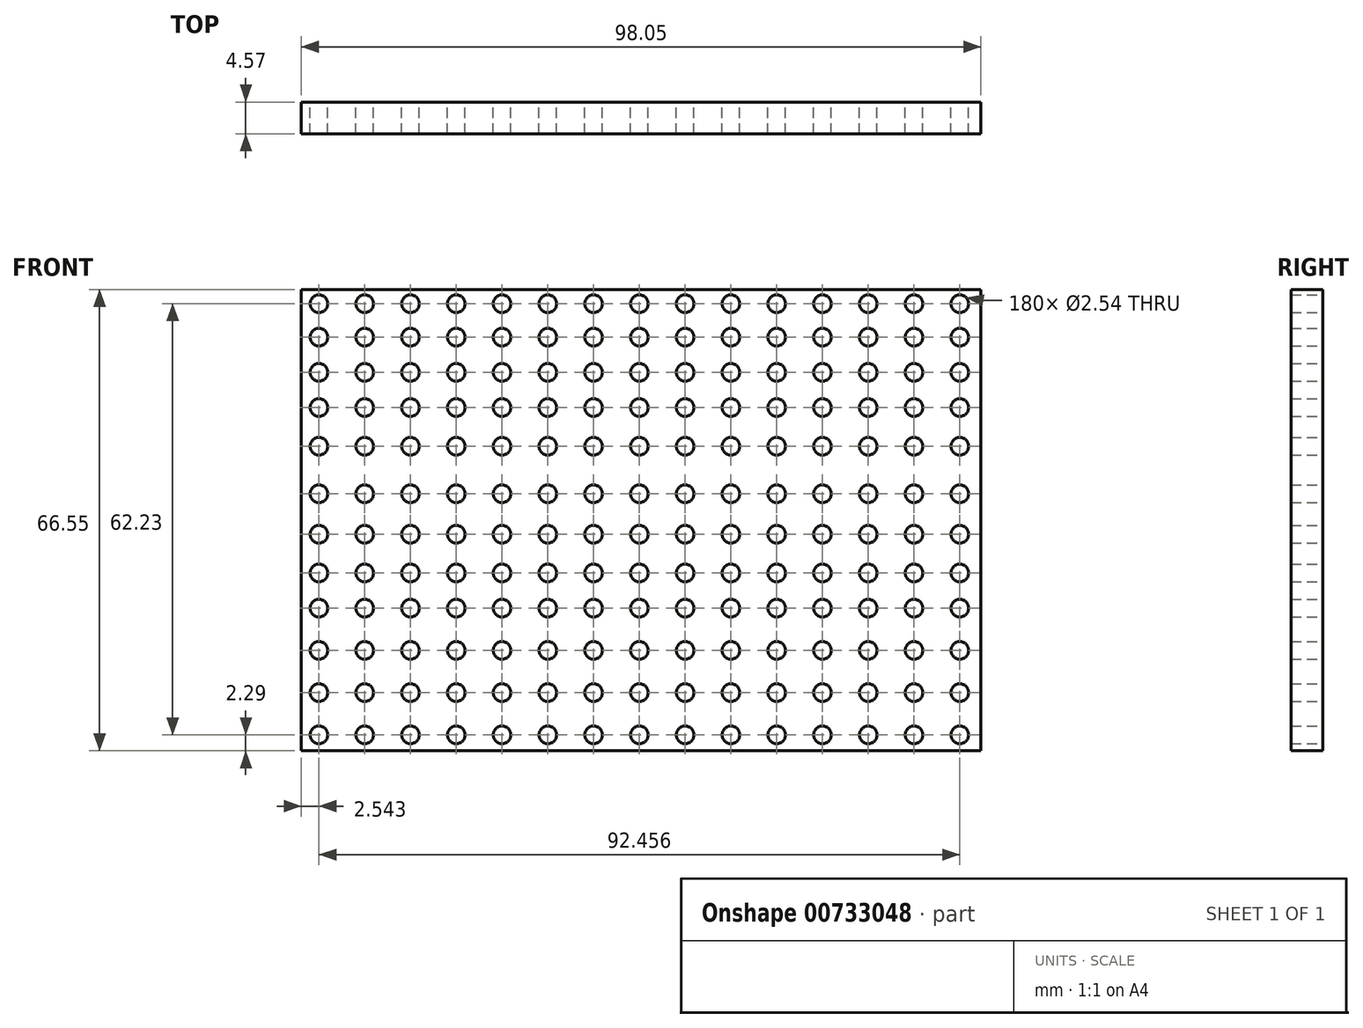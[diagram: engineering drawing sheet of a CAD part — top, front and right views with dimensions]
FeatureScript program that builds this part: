
annotation { "Feature Type Name" : "Feature", "Feature Type Description" : "" }
export const myFeature = defineFeature(function(context is Context, id is Id, definition is map)
    precondition{}
    {
        {
            var Q0;
            Q0=qCreatedBy(makeId("Front.planeOp"),FACE);
            var sketch = newSketch(context, id + "F0", { "sketchPlane" : qUnion([Q0])});
            skLineSegment(sketch, "E0.bottom", {"start": v(-48.39, 32.38) * mm, "end": v(49.66, 32.38) * mm});
            skLineSegment(sketch, "E0.top", {"start": v(-48.39, -34.17) * mm, "end": v(49.66, -34.17) * mm});
            skLineSegment(sketch, "E0.left", {"start": v(-48.39, 32.38) * mm, "end": v(-48.39, -34.17) * mm});
            skLineSegment(sketch, "E0.right", {"start": v(49.66, 32.38) * mm, "end": v(49.66, -34.17) * mm});
            skCircle(sketch, "E1", {"center": v(-45.85, 30.35) * mm, "radius": 1.27 * mm});
            skCircle(sketch, "E2.0.1.0", {"center": v(-45.85, -31.88) * mm, "radius": 1.27 * mm});
            skCircle(sketch, "E2.1.0.0", {"center": v(-39.24, 30.35) * mm, "radius": 1.27 * mm});
            skCircle(sketch, "E2.1.1.0", {"center": v(-39.24, -31.88) * mm, "radius": 1.27 * mm});
            skCircle(sketch, "E2.2.0.0", {"center": v(-32.64, 30.35) * mm, "radius": 1.27 * mm});
            skCircle(sketch, "E2.2.1.0", {"center": v(-32.64, -31.88) * mm, "radius": 1.27 * mm});
            skCircle(sketch, "E2.3.0.0", {"center": v(-26.04, 30.35) * mm, "radius": 1.27 * mm});
            skCircle(sketch, "E2.3.1.0", {"center": v(-26.04, -31.88) * mm, "radius": 1.27 * mm});
            skCircle(sketch, "E2.4.0.0", {"center": v(-19.43, 30.35) * mm, "radius": 1.27 * mm});
            skCircle(sketch, "E2.4.1.0", {"center": v(-19.43, -31.88) * mm, "radius": 1.27 * mm});
            skCircle(sketch, "E2.5.0.0", {"center": v(-12.83, 30.35) * mm, "radius": 1.27 * mm});
            skCircle(sketch, "E2.5.1.0", {"center": v(-12.83, -31.88) * mm, "radius": 1.27 * mm});
            skCircle(sketch, "E2.6.0.0", {"center": v(-6.22, 30.35) * mm, "radius": 1.27 * mm});
            skCircle(sketch, "E2.6.1.0", {"center": v(-6.22, -31.88) * mm, "radius": 1.27 * mm});
            skCircle(sketch, "E2.7.0.0", {"center": v(0.38, 30.35) * mm, "radius": 1.27 * mm});
            skCircle(sketch, "E2.7.1.0", {"center": v(0.38, -31.88) * mm, "radius": 1.27 * mm});
            skCircle(sketch, "E2.8.0.0", {"center": v(6.98, 30.35) * mm, "radius": 1.27 * mm});
            skCircle(sketch, "E2.8.1.0", {"center": v(6.98, -31.88) * mm, "radius": 1.27 * mm});
            skCircle(sketch, "E2.9.0.0", {"center": v(13.59, 30.35) * mm, "radius": 1.27 * mm});
            skCircle(sketch, "E2.9.1.0", {"center": v(13.59, -31.88) * mm, "radius": 1.27 * mm});
            skCircle(sketch, "E2.10.0.0", {"center": v(20.2, 30.35) * mm, "radius": 1.27 * mm});
            skCircle(sketch, "E2.10.1.0", {"center": v(20.2, -31.88) * mm, "radius": 1.27 * mm});
            skCircle(sketch, "E2.11.0.0", {"center": v(26.8, 30.35) * mm, "radius": 1.27 * mm});
            skCircle(sketch, "E2.11.1.0", {"center": v(26.8, -31.88) * mm, "radius": 1.27 * mm});
            skCircle(sketch, "E2.12.0.0", {"center": v(33.4, 30.35) * mm, "radius": 1.27 * mm});
            skCircle(sketch, "E2.12.1.0", {"center": v(33.4, -31.88) * mm, "radius": 1.27 * mm});
            skCircle(sketch, "E2.13.0.0", {"center": v(40, 30.35) * mm, "radius": 1.27 * mm});
            skCircle(sketch, "E2.13.1.0", {"center": v(40, -31.88) * mm, "radius": 1.27 * mm});
            skCircle(sketch, "E2.14.0.0", {"center": v(46.6, 30.35) * mm, "radius": 1.27 * mm});
            skCircle(sketch, "E2.14.1.0", {"center": v(46.6, -31.88) * mm, "radius": 1.27 * mm});
            skLineSegment(sketch, "E2.direction1", {"start": v(-45.85, 30.35) * mm, "end": v(-39.24, 30.35) * mm, "construction": true});
            skLineSegment(sketch, "E2.direction2", {"start": v(-45.85, 30.35) * mm, "end": v(-45.85, -31.88) * mm, "construction": true});
            skCircle(sketch, "E3.0.1.0", {"center": v(-45.85, -25.78) * mm, "radius": 1.27 * mm});
            skCircle(sketch, "E3.1.1.0", {"center": v(-39.24, -25.78) * mm, "radius": 1.27 * mm});
            skCircle(sketch, "E3.2.1.0", {"center": v(-32.64, -25.78) * mm, "radius": 1.27 * mm});
            skCircle(sketch, "E3.3.1.0", {"center": v(-26.04, -25.78) * mm, "radius": 1.27 * mm});
            skCircle(sketch, "E3.4.1.0", {"center": v(-19.43, -25.78) * mm, "radius": 1.27 * mm});
            skCircle(sketch, "E3.5.1.0", {"center": v(-12.83, -25.78) * mm, "radius": 1.27 * mm});
            skCircle(sketch, "E3.6.1.0", {"center": v(-6.22, -25.78) * mm, "radius": 1.27 * mm});
            skCircle(sketch, "E3.7.1.0", {"center": v(0.38, -25.78) * mm, "radius": 1.27 * mm});
            skCircle(sketch, "E3.8.1.0", {"center": v(6.98, -25.78) * mm, "radius": 1.27 * mm});
            skCircle(sketch, "E3.9.1.0", {"center": v(13.59, -25.78) * mm, "radius": 1.27 * mm});
            skCircle(sketch, "E3.10.1.0", {"center": v(20.2, -25.78) * mm, "radius": 1.27 * mm});
            skCircle(sketch, "E3.11.1.0", {"center": v(26.8, -25.78) * mm, "radius": 1.27 * mm});
            skCircle(sketch, "E3.12.1.0", {"center": v(33.4, -25.78) * mm, "radius": 1.27 * mm});
            skCircle(sketch, "E3.13.1.0", {"center": v(40, -25.78) * mm, "radius": 1.27 * mm});
            skCircle(sketch, "E3.14.1.0", {"center": v(46.6, -25.78) * mm, "radius": 1.27 * mm});
            skLineSegment(sketch, "E3.direction2", {"start": v(-45.85, 30.35) * mm, "end": v(-45.85, -25.78) * mm, "construction": true});
            skCircle(sketch, "E4.0.1.0", {"center": v(-45.85, -19.69) * mm, "radius": 1.27 * mm});
            skCircle(sketch, "E4.1.1.0", {"center": v(-39.24, -19.69) * mm, "radius": 1.27 * mm});
            skCircle(sketch, "E4.2.1.0", {"center": v(-32.64, -19.69) * mm, "radius": 1.27 * mm});
            skCircle(sketch, "E4.3.1.0", {"center": v(-26.04, -19.69) * mm, "radius": 1.27 * mm});
            skCircle(sketch, "E4.4.1.0", {"center": v(-19.43, -19.69) * mm, "radius": 1.27 * mm});
            skCircle(sketch, "E4.5.1.0", {"center": v(-12.83, -19.69) * mm, "radius": 1.27 * mm});
            skCircle(sketch, "E4.6.1.0", {"center": v(-6.22, -19.69) * mm, "radius": 1.27 * mm});
            skCircle(sketch, "E4.7.1.0", {"center": v(0.38, -19.69) * mm, "radius": 1.27 * mm});
            skCircle(sketch, "E4.8.1.0", {"center": v(6.98, -19.69) * mm, "radius": 1.27 * mm});
            skCircle(sketch, "E4.9.1.0", {"center": v(13.59, -19.69) * mm, "radius": 1.27 * mm});
            skCircle(sketch, "E4.10.1.0", {"center": v(20.2, -19.69) * mm, "radius": 1.27 * mm});
            skCircle(sketch, "E4.11.1.0", {"center": v(26.8, -19.69) * mm, "radius": 1.27 * mm});
            skCircle(sketch, "E4.12.1.0", {"center": v(33.4, -19.69) * mm, "radius": 1.27 * mm});
            skCircle(sketch, "E4.13.1.0", {"center": v(40, -19.69) * mm, "radius": 1.27 * mm});
            skCircle(sketch, "E4.14.1.0", {"center": v(46.6, -19.69) * mm, "radius": 1.27 * mm});
            skLineSegment(sketch, "E4.direction2", {"start": v(-45.85, 30.35) * mm, "end": v(-45.85, -19.69) * mm, "construction": true});
            skCircle(sketch, "E5.0.1.0", {"center": v(-45.85, -13.6) * mm, "radius": 1.27 * mm});
            skCircle(sketch, "E5.1.1.0", {"center": v(-39.24, -13.6) * mm, "radius": 1.27 * mm});
            skCircle(sketch, "E5.2.1.0", {"center": v(-32.64, -13.6) * mm, "radius": 1.27 * mm});
            skCircle(sketch, "E5.3.1.0", {"center": v(-26.04, -13.6) * mm, "radius": 1.27 * mm});
            skCircle(sketch, "E5.4.1.0", {"center": v(-19.43, -13.6) * mm, "radius": 1.27 * mm});
            skCircle(sketch, "E5.5.1.0", {"center": v(-12.83, -13.6) * mm, "radius": 1.27 * mm});
            skCircle(sketch, "E5.6.1.0", {"center": v(-6.22, -13.6) * mm, "radius": 1.27 * mm});
            skCircle(sketch, "E5.7.1.0", {"center": v(0.38, -13.6) * mm, "radius": 1.27 * mm});
            skCircle(sketch, "E5.8.1.0", {"center": v(6.98, -13.6) * mm, "radius": 1.27 * mm});
            skCircle(sketch, "E5.9.1.0", {"center": v(13.59, -13.6) * mm, "radius": 1.27 * mm});
            skCircle(sketch, "E5.10.1.0", {"center": v(20.2, -13.6) * mm, "radius": 1.27 * mm});
            skCircle(sketch, "E5.11.1.0", {"center": v(26.8, -13.6) * mm, "radius": 1.27 * mm});
            skCircle(sketch, "E5.12.1.0", {"center": v(33.4, -13.6) * mm, "radius": 1.27 * mm});
            skCircle(sketch, "E5.13.1.0", {"center": v(40, -13.6) * mm, "radius": 1.27 * mm});
            skCircle(sketch, "E5.14.1.0", {"center": v(46.6, -13.6) * mm, "radius": 1.27 * mm});
            skLineSegment(sketch, "E5.direction2", {"start": v(-45.85, 30.35) * mm, "end": v(-45.85, -13.6) * mm, "construction": true});
            skCircle(sketch, "E6.0.1.0", {"center": v(-45.85, -8.51) * mm, "radius": 1.27 * mm});
            skCircle(sketch, "E6.1.1.0", {"center": v(-39.24, -8.51) * mm, "radius": 1.27 * mm});
            skCircle(sketch, "E6.2.1.0", {"center": v(-32.64, -8.51) * mm, "radius": 1.27 * mm});
            skCircle(sketch, "E6.3.1.0", {"center": v(-26.04, -8.51) * mm, "radius": 1.27 * mm});
            skCircle(sketch, "E6.4.1.0", {"center": v(-19.43, -8.51) * mm, "radius": 1.27 * mm});
            skCircle(sketch, "E6.5.1.0", {"center": v(-12.83, -8.51) * mm, "radius": 1.27 * mm});
            skCircle(sketch, "E6.6.1.0", {"center": v(-6.22, -8.51) * mm, "radius": 1.27 * mm});
            skCircle(sketch, "E6.7.1.0", {"center": v(0.38, -8.51) * mm, "radius": 1.27 * mm});
            skCircle(sketch, "E6.8.1.0", {"center": v(6.98, -8.51) * mm, "radius": 1.27 * mm});
            skCircle(sketch, "E6.9.1.0", {"center": v(13.59, -8.51) * mm, "radius": 1.27 * mm});
            skCircle(sketch, "E6.10.1.0", {"center": v(20.2, -8.51) * mm, "radius": 1.27 * mm});
            skCircle(sketch, "E6.11.1.0", {"center": v(26.8, -8.51) * mm, "radius": 1.27 * mm});
            skCircle(sketch, "E6.12.1.0", {"center": v(33.4, -8.51) * mm, "radius": 1.27 * mm});
            skCircle(sketch, "E6.13.1.0", {"center": v(40, -8.51) * mm, "radius": 1.27 * mm});
            skCircle(sketch, "E6.14.1.0", {"center": v(46.6, -8.51) * mm, "radius": 1.27 * mm});
            skLineSegment(sketch, "E6.direction2", {"start": v(-45.85, 30.35) * mm, "end": v(-45.85, -8.51) * mm, "construction": true});
            skCircle(sketch, "E7.0.1.0", {"center": v(-45.85, -2.92) * mm, "radius": 1.27 * mm});
            skCircle(sketch, "E7.1.1.0", {"center": v(-39.24, -2.92) * mm, "radius": 1.27 * mm});
            skCircle(sketch, "E7.2.1.0", {"center": v(-32.64, -2.92) * mm, "radius": 1.27 * mm});
            skCircle(sketch, "E7.3.1.0", {"center": v(-26.04, -2.92) * mm, "radius": 1.27 * mm});
            skCircle(sketch, "E7.4.1.0", {"center": v(-19.43, -2.92) * mm, "radius": 1.27 * mm});
            skCircle(sketch, "E7.5.1.0", {"center": v(-12.83, -2.92) * mm, "radius": 1.27 * mm});
            skCircle(sketch, "E7.6.1.0", {"center": v(-6.22, -2.92) * mm, "radius": 1.27 * mm});
            skCircle(sketch, "E7.7.1.0", {"center": v(0.38, -2.92) * mm, "radius": 1.27 * mm});
            skCircle(sketch, "E7.8.1.0", {"center": v(6.98, -2.92) * mm, "radius": 1.27 * mm});
            skCircle(sketch, "E7.9.1.0", {"center": v(13.59, -2.92) * mm, "radius": 1.27 * mm});
            skCircle(sketch, "E7.10.1.0", {"center": v(20.2, -2.92) * mm, "radius": 1.27 * mm});
            skCircle(sketch, "E7.11.1.0", {"center": v(26.8, -2.92) * mm, "radius": 1.27 * mm});
            skCircle(sketch, "E7.12.1.0", {"center": v(33.4, -2.92) * mm, "radius": 1.27 * mm});
            skCircle(sketch, "E7.13.1.0", {"center": v(40, -2.92) * mm, "radius": 1.27 * mm});
            skCircle(sketch, "E7.14.1.0", {"center": v(46.6, -2.92) * mm, "radius": 1.27 * mm});
            skLineSegment(sketch, "E7.direction2", {"start": v(-45.85, 30.35) * mm, "end": v(-45.85, -2.92) * mm, "construction": true});
            skCircle(sketch, "E8.0.1.0", {"center": v(-45.85, 2.92) * mm, "radius": 1.27 * mm});
            skCircle(sketch, "E8.1.1.0", {"center": v(-39.24, 2.92) * mm, "radius": 1.27 * mm});
            skCircle(sketch, "E8.2.1.0", {"center": v(-32.64, 2.92) * mm, "radius": 1.27 * mm});
            skCircle(sketch, "E8.3.1.0", {"center": v(-26.04, 2.92) * mm, "radius": 1.27 * mm});
            skCircle(sketch, "E8.4.1.0", {"center": v(-19.43, 2.92) * mm, "radius": 1.27 * mm});
            skCircle(sketch, "E8.5.1.0", {"center": v(-12.83, 2.92) * mm, "radius": 1.27 * mm});
            skCircle(sketch, "E8.6.1.0", {"center": v(-6.22, 2.92) * mm, "radius": 1.27 * mm});
            skCircle(sketch, "E8.7.1.0", {"center": v(0.38, 2.92) * mm, "radius": 1.27 * mm});
            skCircle(sketch, "E8.8.1.0", {"center": v(6.98, 2.92) * mm, "radius": 1.27 * mm});
            skCircle(sketch, "E8.9.1.0", {"center": v(13.59, 2.92) * mm, "radius": 1.27 * mm});
            skCircle(sketch, "E8.10.1.0", {"center": v(20.2, 2.92) * mm, "radius": 1.27 * mm});
            skCircle(sketch, "E8.11.1.0", {"center": v(26.8, 2.92) * mm, "radius": 1.27 * mm});
            skCircle(sketch, "E8.12.1.0", {"center": v(33.4, 2.92) * mm, "radius": 1.27 * mm});
            skCircle(sketch, "E8.13.1.0", {"center": v(40, 2.92) * mm, "radius": 1.27 * mm});
            skCircle(sketch, "E8.14.1.0", {"center": v(46.6, 2.92) * mm, "radius": 1.27 * mm});
            skLineSegment(sketch, "E8.direction2", {"start": v(-45.85, 30.35) * mm, "end": v(-45.85, 2.92) * mm, "construction": true});
            skCircle(sketch, "E9.0.1.0", {"center": v(-45.85, 9.78) * mm, "radius": 1.27 * mm});
            skCircle(sketch, "E9.1.1.0", {"center": v(-39.24, 9.78) * mm, "radius": 1.27 * mm});
            skCircle(sketch, "E9.2.1.0", {"center": v(-32.64, 9.78) * mm, "radius": 1.27 * mm});
            skCircle(sketch, "E9.3.1.0", {"center": v(-26.04, 9.78) * mm, "radius": 1.27 * mm});
            skCircle(sketch, "E9.4.1.0", {"center": v(-19.43, 9.78) * mm, "radius": 1.27 * mm});
            skCircle(sketch, "E9.5.1.0", {"center": v(-12.83, 9.78) * mm, "radius": 1.27 * mm});
            skCircle(sketch, "E9.6.1.0", {"center": v(-6.22, 9.78) * mm, "radius": 1.27 * mm});
            skCircle(sketch, "E9.7.1.0", {"center": v(0.38, 9.78) * mm, "radius": 1.27 * mm});
            skCircle(sketch, "E9.8.1.0", {"center": v(6.98, 9.78) * mm, "radius": 1.27 * mm});
            skCircle(sketch, "E9.9.1.0", {"center": v(13.59, 9.78) * mm, "radius": 1.27 * mm});
            skCircle(sketch, "E9.10.1.0", {"center": v(20.2, 9.78) * mm, "radius": 1.27 * mm});
            skCircle(sketch, "E9.11.1.0", {"center": v(26.8, 9.78) * mm, "radius": 1.27 * mm});
            skCircle(sketch, "E9.12.1.0", {"center": v(33.4, 9.78) * mm, "radius": 1.27 * mm});
            skCircle(sketch, "E9.13.1.0", {"center": v(40, 9.78) * mm, "radius": 1.27 * mm});
            skCircle(sketch, "E9.14.1.0", {"center": v(46.6, 9.78) * mm, "radius": 1.27 * mm});
            skLineSegment(sketch, "E9.direction2", {"start": v(-45.85, 30.35) * mm, "end": v(-45.85, 9.78) * mm, "construction": true});
            skCircle(sketch, "E10.0.1.0", {"center": v(-45.85, 15.36) * mm, "radius": 1.27 * mm});
            skCircle(sketch, "E10.1.1.0", {"center": v(-39.24, 15.36) * mm, "radius": 1.27 * mm});
            skCircle(sketch, "E10.2.1.0", {"center": v(-32.64, 15.36) * mm, "radius": 1.27 * mm});
            skCircle(sketch, "E10.3.1.0", {"center": v(-26.04, 15.36) * mm, "radius": 1.27 * mm});
            skCircle(sketch, "E10.4.1.0", {"center": v(-19.43, 15.36) * mm, "radius": 1.27 * mm});
            skCircle(sketch, "E10.5.1.0", {"center": v(-12.83, 15.36) * mm, "radius": 1.27 * mm});
            skCircle(sketch, "E10.6.1.0", {"center": v(-6.22, 15.36) * mm, "radius": 1.27 * mm});
            skCircle(sketch, "E10.7.1.0", {"center": v(0.38, 15.36) * mm, "radius": 1.27 * mm});
            skCircle(sketch, "E10.8.1.0", {"center": v(6.98, 15.36) * mm, "radius": 1.27 * mm});
            skCircle(sketch, "E10.9.1.0", {"center": v(13.59, 15.36) * mm, "radius": 1.27 * mm});
            skCircle(sketch, "E10.10.1.0", {"center": v(20.2, 15.36) * mm, "radius": 1.27 * mm});
            skCircle(sketch, "E10.11.1.0", {"center": v(26.8, 15.36) * mm, "radius": 1.27 * mm});
            skCircle(sketch, "E10.12.1.0", {"center": v(33.4, 15.36) * mm, "radius": 1.27 * mm});
            skCircle(sketch, "E10.13.1.0", {"center": v(40, 15.36) * mm, "radius": 1.27 * mm});
            skCircle(sketch, "E10.14.1.0", {"center": v(46.6, 15.36) * mm, "radius": 1.27 * mm});
            skLineSegment(sketch, "E10.direction2", {"start": v(-45.85, 30.35) * mm, "end": v(-45.85, 15.36) * mm, "construction": true});
            skCircle(sketch, "E11.0.1.0", {"center": v(-45.85, 20.44) * mm, "radius": 1.27 * mm});
            skCircle(sketch, "E11.1.1.0", {"center": v(-39.24, 20.44) * mm, "radius": 1.27 * mm});
            skCircle(sketch, "E11.2.1.0", {"center": v(-32.64, 20.44) * mm, "radius": 1.27 * mm});
            skCircle(sketch, "E11.3.1.0", {"center": v(-26.04, 20.44) * mm, "radius": 1.27 * mm});
            skCircle(sketch, "E11.4.1.0", {"center": v(-19.43, 20.44) * mm, "radius": 1.27 * mm});
            skCircle(sketch, "E11.5.1.0", {"center": v(-12.83, 20.44) * mm, "radius": 1.27 * mm});
            skCircle(sketch, "E11.6.1.0", {"center": v(-6.22, 20.44) * mm, "radius": 1.27 * mm});
            skCircle(sketch, "E11.7.1.0", {"center": v(0.38, 20.44) * mm, "radius": 1.27 * mm});
            skCircle(sketch, "E11.8.1.0", {"center": v(6.98, 20.44) * mm, "radius": 1.27 * mm});
            skCircle(sketch, "E11.9.1.0", {"center": v(13.59, 20.44) * mm, "radius": 1.27 * mm});
            skCircle(sketch, "E11.10.1.0", {"center": v(20.2, 20.44) * mm, "radius": 1.27 * mm});
            skCircle(sketch, "E11.11.1.0", {"center": v(26.8, 20.44) * mm, "radius": 1.27 * mm});
            skCircle(sketch, "E11.12.1.0", {"center": v(33.4, 20.44) * mm, "radius": 1.27 * mm});
            skCircle(sketch, "E11.13.1.0", {"center": v(40, 20.44) * mm, "radius": 1.27 * mm});
            skCircle(sketch, "E11.14.1.0", {"center": v(46.6, 20.44) * mm, "radius": 1.27 * mm});
            skLineSegment(sketch, "E11.direction2", {"start": v(-45.85, 30.35) * mm, "end": v(-45.85, 20.44) * mm, "construction": true});
            skCircle(sketch, "E12.0.1.0", {"center": v(-45.85, 25.52) * mm, "radius": 1.27 * mm});
            skCircle(sketch, "E12.1.1.0", {"center": v(-39.24, 25.52) * mm, "radius": 1.27 * mm});
            skCircle(sketch, "E12.2.1.0", {"center": v(-32.64, 25.52) * mm, "radius": 1.27 * mm});
            skCircle(sketch, "E12.3.1.0", {"center": v(-26.04, 25.52) * mm, "radius": 1.27 * mm});
            skCircle(sketch, "E12.4.1.0", {"center": v(-19.43, 25.52) * mm, "radius": 1.27 * mm});
            skCircle(sketch, "E12.5.1.0", {"center": v(-12.83, 25.52) * mm, "radius": 1.27 * mm});
            skCircle(sketch, "E12.6.1.0", {"center": v(-6.22, 25.52) * mm, "radius": 1.27 * mm});
            skCircle(sketch, "E12.7.1.0", {"center": v(0.38, 25.52) * mm, "radius": 1.27 * mm});
            skCircle(sketch, "E12.8.1.0", {"center": v(6.98, 25.52) * mm, "radius": 1.27 * mm});
            skCircle(sketch, "E12.9.1.0", {"center": v(13.59, 25.52) * mm, "radius": 1.27 * mm});
            skCircle(sketch, "E12.10.1.0", {"center": v(20.2, 25.52) * mm, "radius": 1.27 * mm});
            skCircle(sketch, "E12.11.1.0", {"center": v(26.8, 25.52) * mm, "radius": 1.27 * mm});
            skCircle(sketch, "E12.12.1.0", {"center": v(33.4, 25.52) * mm, "radius": 1.27 * mm});
            skCircle(sketch, "E12.13.1.0", {"center": v(40, 25.52) * mm, "radius": 1.27 * mm});
            skCircle(sketch, "E12.14.1.0", {"center": v(46.6, 25.52) * mm, "radius": 1.27 * mm});
            skLineSegment(sketch, "E12.direction2", {"start": v(-45.85, 30.35) * mm, "end": v(-45.85, 25.52) * mm, "construction": true});
            skSolve(sketch);
        }
        {
            var Q0;
            Q0=makeQuery(id+"F0.imprint","IMPRINT",FACE,{"disambiguationData":[TD([[makeQuery(id+"F0.imprint","IMPRINT",EDGE,{"derivedFrom":sQuery(id+"F0.wireOp",EDGE,"E0.bottom")}),-1.0]])]});
            extrude(context, id + "F1", {"entities" : qUnion([Q0]), "depth" : 4.57 * mm, "offsetDistance" : 25.4 * mm});
        }
    });
